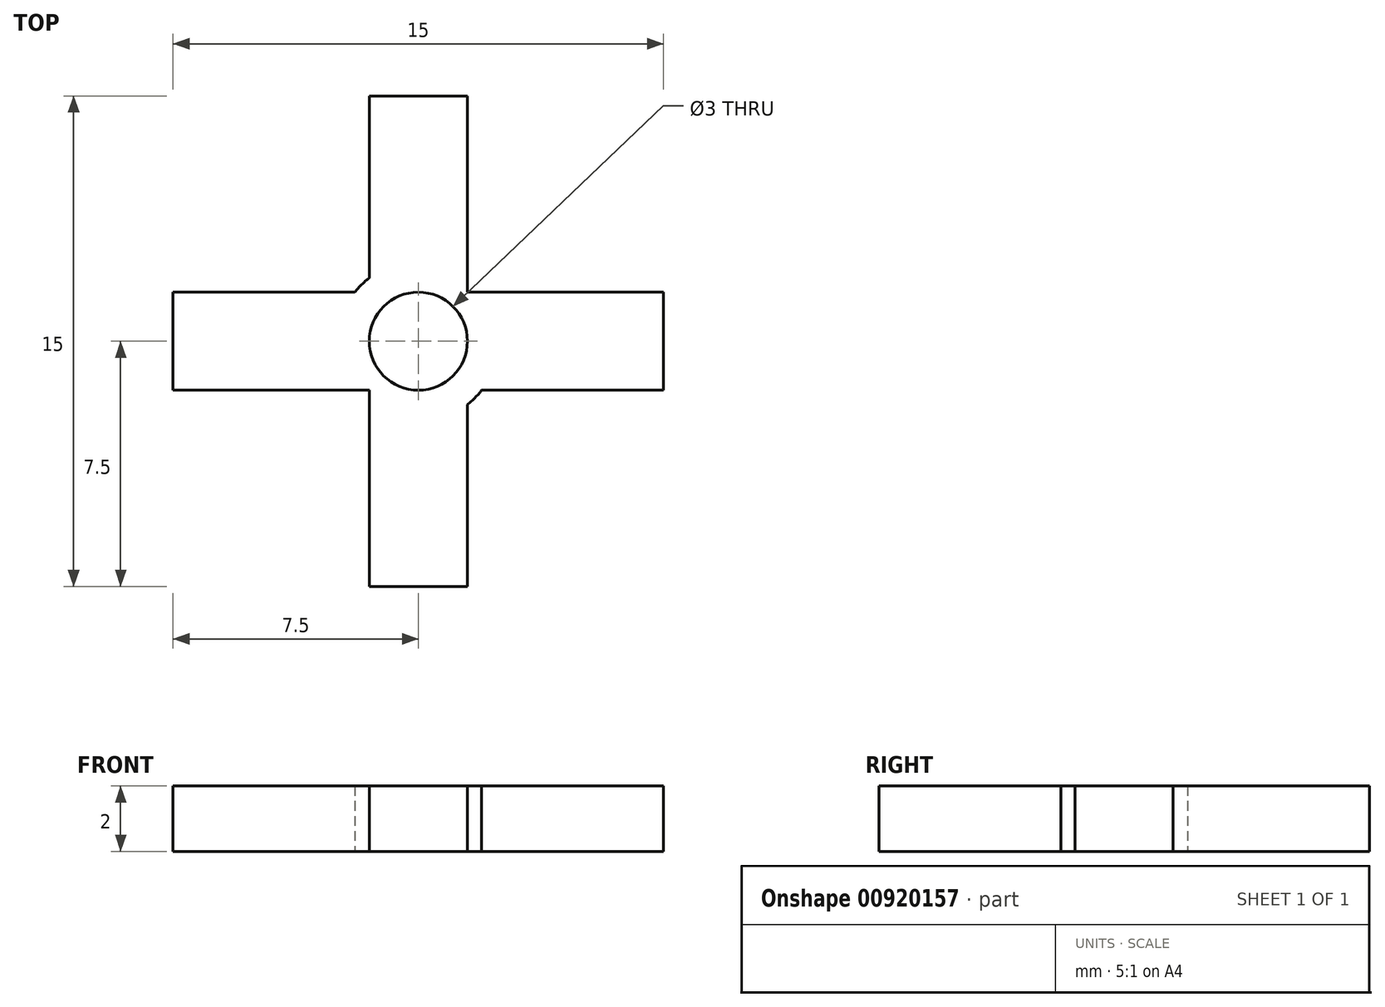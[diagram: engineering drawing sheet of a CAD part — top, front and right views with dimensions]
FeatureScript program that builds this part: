
annotation { "Feature Type Name" : "Feature", "Feature Type Description" : "" }
export const myFeature = defineFeature(function(context is Context, id is Id, definition is map)
    precondition{}
    {
        {
            var Q0;
            Q0=qCreatedBy(makeId("Top.planeOp"),FACE);
            var sketch = newSketch(context, id + "F0", { "sketchPlane" : qUnion([Q0])});
            skCircle(sketch, "E0", {"center": v(0, 0) * mm, "radius": 2.45 * mm});
            skLineSegment(sketch, "E1.bottom", {"start": v(-7.5, 1.5) * mm, "end": v(7.5, 1.5) * mm});
            skLineSegment(sketch, "E1.top", {"start": v(-7.5, -1.5) * mm, "end": v(7.5, -1.5) * mm});
            skLineSegment(sketch, "E1.left", {"start": v(-7.5, 1.5) * mm, "end": v(-7.5, -1.5) * mm});
            skLineSegment(sketch, "E1.right", {"start": v(7.5, 1.5) * mm, "end": v(7.5, -1.5) * mm});
            skLineSegment(sketch, "E2", {"start": v(-7.5, 1.5) * mm, "end": v(7.5, -1.5) * mm, "construction": true});
            skLineSegment(sketch, "E3", {"start": v(-7.5, -1.5) * mm, "end": v(7.5, 1.5) * mm, "construction": true});
            skLineSegment(sketch, "E4.bottom", {"start": v(-1.5, 7.5) * mm, "end": v(1.5, 7.5) * mm});
            skLineSegment(sketch, "E4.top", {"start": v(-1.5, -7.5) * mm, "end": v(1.5, -7.5) * mm});
            skLineSegment(sketch, "E4.left", {"start": v(-1.5, 7.5) * mm, "end": v(-1.5, -7.5) * mm});
            skLineSegment(sketch, "E4.right", {"start": v(1.5, 7.5) * mm, "end": v(1.5, -7.5) * mm});
            skLineSegment(sketch, "E5", {"start": v(-1.5, 7.5) * mm, "end": v(1.5, -7.5) * mm, "construction": true});
            skLineSegment(sketch, "E6", {"start": v(-1.5, -7.5) * mm, "end": v(1.5, 7.5) * mm, "construction": true});
            skSolve(sketch);
        }
        {
            var Q0;
            {var subQ5=sQuery(id+"F0.wireOp",EDGE,"E1.left");Q0=makeQuery(id+"F0.imprint","IMPRINT",FACE,{"disambiguationData":[TD([[makeQuery(id+"F0.imprint","IMPRINT",EDGE,{"derivedFrom":subQ5}),1.0]])]});}
            var Q1;
            {var subQ0=sQuery(id+"F0.wireOp",EDGE,"E4.left");var subQ1=sQuery(id+"F0.wireOp",EDGE,"E1.bottom");var subQ2=makeQuery(id+"F0.imprint","INTERSECT",VERTEX,{"derivedFrom":[subQ1,subQ0]});Q1=makeQuery(id+"F0.imprint","IMPRINT",FACE,{"disambiguationData":[TD([[makeQuery(id+"F0.imprint","IMPRINT",EDGE,{"disambiguationData":[TD([[subQ2,-1.0]])],"derivedFrom":subQ1}),-1.0]])]});}
            var Q2;
            {var subQ0=sQuery(id+"F0.wireOp",EDGE,"E1.bottom");var subQ1=sQuery(id+"F0.wireOp",EDGE,"E0");var subQ2=makeQuery(id+"F0.imprint","INTERSECT",VERTEX,{"disambiguationData":[OD(1.0)],"derivedFrom":[subQ1,subQ0]});Q2=makeQuery(id+"F0.imprint","IMPRINT",FACE,{"disambiguationData":[TD([[makeQuery(id+"F0.imprint","IMPRINT",EDGE,{"disambiguationData":[TD([[subQ2,-1.0]])],"derivedFrom":subQ1}),1.0]])]});}
            var Q3;
            {var subQ5=sQuery(id+"F0.wireOp",EDGE,"E1.right");Q3=makeQuery(id+"F0.imprint","IMPRINT",FACE,{"disambiguationData":[TD([[makeQuery(id+"F0.imprint","IMPRINT",EDGE,{"derivedFrom":subQ5}),-1.0]])]});}
            var Q4;
            {var subQ5=sQuery(id+"F0.wireOp",EDGE,"E4.top");Q4=makeQuery(id+"F0.imprint","IMPRINT",FACE,{"disambiguationData":[TD([[makeQuery(id+"F0.imprint","IMPRINT",EDGE,{"derivedFrom":subQ5}),1.0]])]});}
            var Q5;
            {var subQ0=sQuery(id+"F0.wireOp",EDGE,"E4.right");var subQ1=sQuery(id+"F0.wireOp",EDGE,"E0");var subQ2=makeQuery(id+"F0.imprint","INTERSECT",VERTEX,{"disambiguationData":[OD(0.0)],"derivedFrom":[subQ1,subQ0]});Q5=makeQuery(id+"F0.imprint","IMPRINT",FACE,{"disambiguationData":[TD([[makeQuery(id+"F0.imprint","IMPRINT",EDGE,{"disambiguationData":[TD([[subQ2,-1.0]])],"derivedFrom":subQ1}),1.0]])]});}
            var Q6;
            {var subQ0=sQuery(id+"F0.wireOp",EDGE,"E1.bottom");var subQ1=sQuery(id+"F0.wireOp",EDGE,"E0");var subQ2=makeQuery(id+"F0.imprint","INTERSECT",VERTEX,{"disambiguationData":[OD(0.0)],"derivedFrom":[subQ1,subQ0]});Q6=makeQuery(id+"F0.imprint","IMPRINT",FACE,{"disambiguationData":[TD([[makeQuery(id+"F0.imprint","IMPRINT",EDGE,{"disambiguationData":[TD([[subQ2,1.0]])],"derivedFrom":subQ1}),1.0]])]});}
            var Q7;
            {var subQ5=sQuery(id+"F0.wireOp",EDGE,"E4.bottom");Q7=makeQuery(id+"F0.imprint","IMPRINT",FACE,{"disambiguationData":[TD([[makeQuery(id+"F0.imprint","IMPRINT",EDGE,{"derivedFrom":subQ5}),-1.0]])]});}
            var Q8;
            {var subQ0=sQuery(id+"F0.wireOp",EDGE,"E4.left");var subQ1=sQuery(id+"F0.wireOp",EDGE,"E0");var subQ2=makeQuery(id+"F0.imprint","INTERSECT",VERTEX,{"disambiguationData":[OD(1.0)],"derivedFrom":[subQ1,subQ0]});Q8=makeQuery(id+"F0.imprint","IMPRINT",FACE,{"disambiguationData":[TD([[makeQuery(id+"F0.imprint","IMPRINT",EDGE,{"disambiguationData":[TD([[subQ2,-1.0]])],"derivedFrom":subQ1}),1.0]])]});}
            var Q9;
            {var subQ0=sQuery(id+"F0.wireOp",EDGE,"E1.top");var subQ1=sQuery(id+"F0.wireOp",EDGE,"E0");var subQ2=makeQuery(id+"F0.imprint","INTERSECT",VERTEX,{"disambiguationData":[OD(0.0)],"derivedFrom":[subQ1,subQ0]});Q9=makeQuery(id+"F0.imprint","IMPRINT",FACE,{"disambiguationData":[TD([[makeQuery(id+"F0.imprint","IMPRINT",EDGE,{"disambiguationData":[TD([[subQ2,-1.0]])],"derivedFrom":subQ1}),1.0]])]});}
            var Q10;
            {var subQ0=sQuery(id+"F0.wireOp",EDGE,"E4.right");var subQ1=sQuery(id+"F0.wireOp",EDGE,"E0");var subQ2=makeQuery(id+"F0.imprint","INTERSECT",VERTEX,{"disambiguationData":[OD(0.0)],"derivedFrom":[subQ1,subQ0]});Q10=makeQuery(id+"F0.imprint","IMPRINT",FACE,{"disambiguationData":[TD([[makeQuery(id+"F0.imprint","IMPRINT",EDGE,{"disambiguationData":[TD([[subQ2,1.0]])],"derivedFrom":subQ1}),1.0]])]});}
            var Q11;
            {var subQ0=sQuery(id+"F0.wireOp",EDGE,"E4.right");var subQ1=sQuery(id+"F0.wireOp",EDGE,"E0");var subQ2=makeQuery(id+"F0.imprint","INTERSECT",VERTEX,{"disambiguationData":[OD(1.0)],"derivedFrom":[subQ1,subQ0]});Q11=makeQuery(id+"F0.imprint","IMPRINT",FACE,{"disambiguationData":[TD([[makeQuery(id+"F0.imprint","IMPRINT",EDGE,{"disambiguationData":[TD([[subQ2,-1.0]])],"derivedFrom":subQ1}),1.0]])]});}
            var Q12;
            {var subQ0=sQuery(id+"F0.wireOp",EDGE,"E4.left");var subQ1=sQuery(id+"F0.wireOp",EDGE,"E0");var subQ2=makeQuery(id+"F0.imprint","INTERSECT",VERTEX,{"disambiguationData":[OD(0.0)],"derivedFrom":[subQ1,subQ0]});Q12=makeQuery(id+"F0.imprint","IMPRINT",FACE,{"disambiguationData":[TD([[makeQuery(id+"F0.imprint","IMPRINT",EDGE,{"disambiguationData":[TD([[subQ2,-1.0]])],"derivedFrom":subQ1}),1.0]])]});}
            extrude(context, id + "F1", {"entities" : qUnion([Q0, Q1, Q2, Q3, Q4, Q5, Q6, Q7, Q8, Q9, Q10, Q11, Q12]), "depth" : 2 * mm, "offsetDistance" : 25 * mm});
        }
        {
            var Q0;
            Q0=makeQuery(id+"F1.opExtrude","CAP_FACE",FACE,{"disambiguationData":[OSD([sQuery(id+"F0.wireOp",EDGE,"E0"),sQuery(id+"F0.wireOp",EDGE,"E1.bottom"),sQuery(id+"F0.wireOp",EDGE,"E1.top"),sQuery(id+"F0.wireOp",EDGE,"E1.left"),sQuery(id+"F0.wireOp",EDGE,"E1.right"),sQuery(id+"F0.wireOp",EDGE,"E4.bottom"),sQuery(id+"F0.wireOp",EDGE,"E4.top"),sQuery(id+"F0.wireOp",EDGE,"E4.left"),sQuery(id+"F0.wireOp",EDGE,"E4.right")])],"isStart":false});
            var sketch = newSketch(context, id + "F2", { "sketchPlane" : qUnion([Q0])});
            skCircle(sketch, "E7", {"center": v(0, 0) * mm, "radius": 1.5 * mm});
            skSolve(sketch);
        }
        {
            var Q0;
            Q0=makeQuery(id+"F2.imprint","IMPRINT",FACE,{"disambiguationData":[TD([[makeQuery(id+"F2.imprint","IMPRINT",EDGE,{"derivedFrom":sQuery(id+"F2.wireOp",EDGE,"E7")}),1.0]])]});
            extrude(context, id + "F3", {"entities" : qUnion([Q0]), "operationType" : NewBodyOperationType.REMOVE, "endBound" : BoundingType.THROUGH_ALL, "oppositeDirection" : true, "depth" : 25 * mm, "offsetDistance" : 25 * mm});
        }
    });
